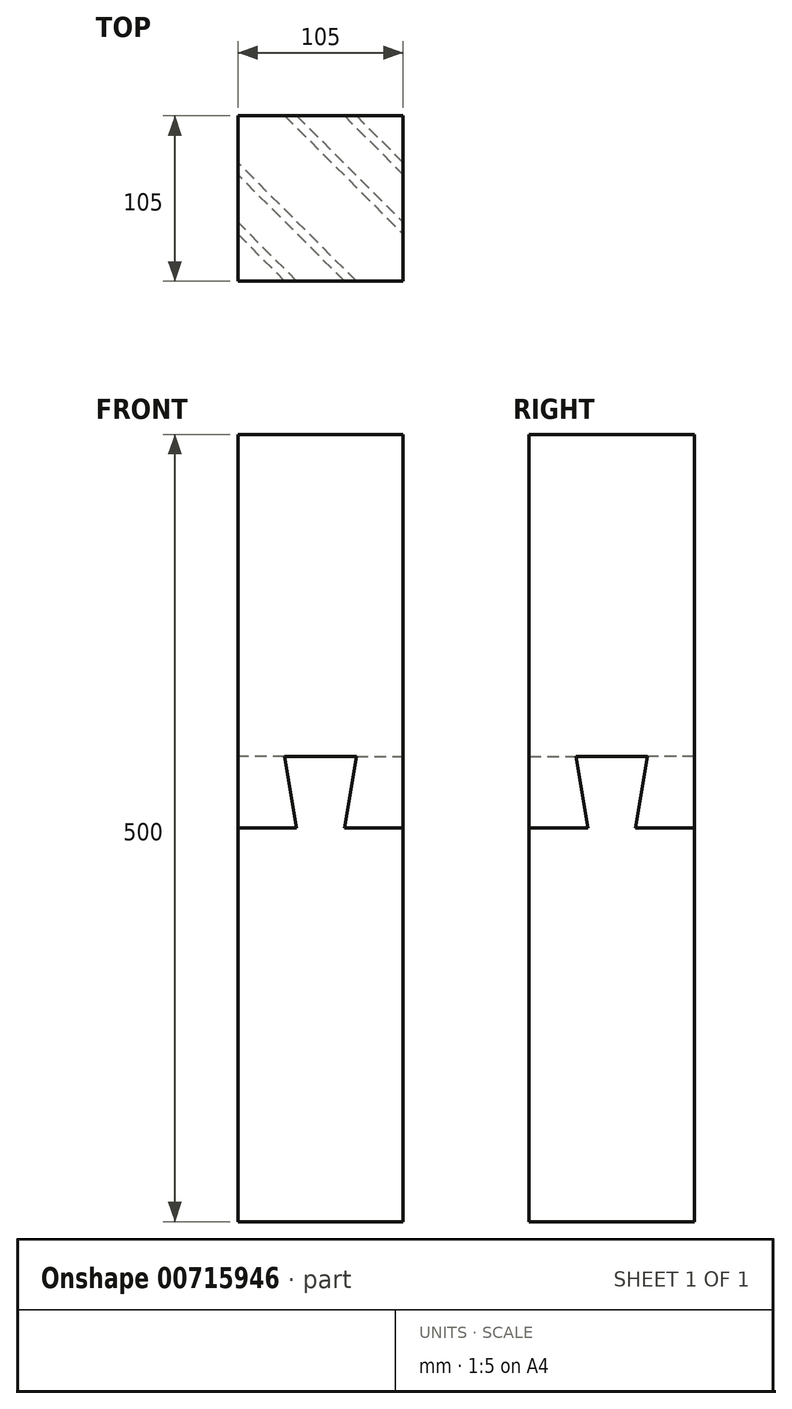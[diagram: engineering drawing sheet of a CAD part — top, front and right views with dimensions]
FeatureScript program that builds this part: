
annotation { "Feature Type Name" : "Feature", "Feature Type Description" : "" }
export const myFeature = defineFeature(function(context is Context, id is Id, definition is map)
    precondition{}
    {
        {
            var Q0;
            Q0=qCreatedBy(makeId("Top.planeOp"),FACE);
            var sketch = newSketch(context, id + "F0", { "sketchPlane" : qUnion([Q0])});
            skLineSegment(sketch, "E0.bottom", {"start": v(52.5, 52.5) * mm, "end": v(-52.5, 52.5) * mm});
            skLineSegment(sketch, "E0.top", {"start": v(52.5, -52.5) * mm, "end": v(-52.5, -52.5) * mm});
            skLineSegment(sketch, "E0.left", {"start": v(52.5, 52.5) * mm, "end": v(52.5, -52.5) * mm});
            skLineSegment(sketch, "E0.right", {"start": v(-52.5, 52.5) * mm, "end": v(-52.5, -52.5) * mm});
            skPoint(sketch, "E0.middle", {"position": v(0, 0) * mm});
            skSolve(sketch);
        }
        {
            var Q0;
            Q0=makeQuery(id+"F0.imprint","IMPRINT",FACE,{"disambiguationData":[TD([[makeQuery(id+"F0.imprint","IMPRINT",EDGE,{"derivedFrom":sQuery(id+"F0.wireOp",EDGE,"E0.bottom")}),1.0]])]});
            extrude(context, id + "F1", {"entities" : qUnion([Q0]), "oppositeDirection" : true, "depth" : 250 * mm, "offsetDistance" : 25 * mm});
        }
        {
            var Q0;
            Q0=makeQuery(id+"F1.opExtrude","SWEPT_FACE",FACE,{"disambiguationData":[OSD([sQuery(id+"F0.wireOp",EDGE,"E0.top")])]});
            var sketch = newSketch(context, id + "F2", { "sketchPlane" : qUnion([Q0])});
            skLineSegment(sketch, "E1", {"start": v(-22.73, 45.45) * mm, "end": v(22.73, 45.45) * mm});
            skLineSegment(sketch, "E2", {"start": v(22.73, 45.45) * mm, "end": v(15.15, 0) * mm});
            skLineSegment(sketch, "E3", {"start": v(15.15, 0) * mm, "end": v(-15.15, 0) * mm});
            skLineSegment(sketch, "E4", {"start": v(-15.15, 0) * mm, "end": v(-22.73, 45.45) * mm});
            skSolve(sketch);
        }
        {
            var Q0;
            Q0=makeQuery(id+"F1.opExtrude","SWEPT_FACE",FACE,{"disambiguationData":[OSD([sQuery(id+"F0.wireOp",EDGE,"E0.right")])]});
            var sketch = newSketch(context, id + "F3", { "sketchPlane" : qUnion([Q0])});
            skLineSegment(sketch, "E5", {"start": v(-22.72, 45.45) * mm, "end": v(22.73, 45.45) * mm});
            skLineSegment(sketch, "E6", {"start": v(22.73, 45.45) * mm, "end": v(15.15, 0) * mm});
            skLineSegment(sketch, "E7", {"start": v(15.15, 0) * mm, "end": v(-15.15, 0) * mm});
            skLineSegment(sketch, "E8", {"start": v(-15.15, 0) * mm, "end": v(-22.72, 45.45) * mm});
            skSolve(sketch);
        }
        {
            var Q1;
            Q1=makeQuery(id+"F2.imprint","IMPRINT",FACE,{"disambiguationData":[TD([[makeQuery(id+"F2.imprint","IMPRINT",EDGE,{"derivedFrom":sQuery(id+"F2.wireOp",EDGE,"E1")}),-1.0]])]});
            var Q2;
            Q2=makeQuery(id+"F3.imprint","IMPRINT",FACE,{"disambiguationData":[TD([[makeQuery(id+"F3.imprint","IMPRINT",EDGE,{"derivedFrom":sQuery(id+"F3.wireOp",EDGE,"E5")}),-1.0]])]});
            loft(context, id + "F4", {"operationType" : NewBodyOperationType.ADD, "sheetProfilesArray" : [{ "sheetProfileEntities" : qUnion([Q1]) }, { "sheetProfileEntities" : qUnion([Q2]) }]});
        }
        {
            var Q0;
            Q0=makeQuery(id+"F1.opExtrude","SWEPT_FACE",FACE,{"disambiguationData":[OSD([sQuery(id+"F0.wireOp",EDGE,"E0.bottom")])]});
            var sketch = newSketch(context, id + "F5", { "sketchPlane" : qUnion([Q0])});
            skLineSegment(sketch, "E9.0", {"start": v(15.15, 0) * mm, "end": v(22.73, 45.45) * mm});
            skLineSegment(sketch, "E10.0", {"start": v(22.73, 45.45) * mm, "end": v(-22.73, 45.45) * mm});
            skLineSegment(sketch, "E11.0", {"start": v(-22.73, 45.45) * mm, "end": v(-15.15, 0) * mm});
            skSolve(sketch);
        }
        {
            var Q0;
            Q0=makeQuery(id+"F1.opExtrude","SWEPT_FACE",FACE,{"disambiguationData":[OSD([sQuery(id+"F0.wireOp",EDGE,"E0.left")])]});
            var sketch = newSketch(context, id + "F6", { "sketchPlane" : qUnion([Q0])});
            skLineSegment(sketch, "E12.0", {"start": v(-15.15, 0) * mm, "end": v(-22.73, 45.45) * mm});
            skLineSegment(sketch, "E13.0", {"start": v(-22.73, 45.45) * mm, "end": v(22.72, 45.45) * mm});
            skLineSegment(sketch, "E14.0", {"start": v(22.73, 45.45) * mm, "end": v(15.15, 0) * mm});
            skSolve(sketch);
        }
        {
            var Q1;
            {var subQ0=sQuery(id+"F5.wireOp",EDGE,"E9.0");Q1=makeQuery(id+"F5.imprint","IMPRINT",FACE,{"disambiguationData":[TD([[makeQuery(id+"F5.imprint","IMPRINT",EDGE,{"derivedFrom":subQ0}),1.0]])]});}
            var Q2;
            {var subQ0=sQuery(id+"F6.wireOp",EDGE,"E12.0");Q2=makeQuery(id+"F6.imprint","IMPRINT",FACE,{"disambiguationData":[TD([[makeQuery(id+"F6.imprint","IMPRINT",EDGE,{"derivedFrom":subQ0}),-1.0]])]});}
            loft(context, id + "F7", {"operationType" : NewBodyOperationType.ADD, "sheetProfilesArray" : [{ "sheetProfileEntities" : qUnion([Q1]) }, { "sheetProfileEntities" : qUnion([Q2]) }]});
        }
        {
            var Q0;
            Q0=qCreatedBy(makeId("Top.planeOp"),FACE);
            var sketch = newSketch(context, id + "F8", { "sketchPlane" : qUnion([Q0])});
            skLineSegment(sketch, "E15.bottom", {"start": v(-52.5, -52.5) * mm, "end": v(52.5, -52.5) * mm});
            skLineSegment(sketch, "E15.top", {"start": v(-52.5, 52.5) * mm, "end": v(52.5, 52.5) * mm});
            skLineSegment(sketch, "E15.left", {"start": v(-52.5, -52.5) * mm, "end": v(-52.5, 52.5) * mm});
            skLineSegment(sketch, "E15.right", {"start": v(52.5, -52.5) * mm, "end": v(52.5, 52.5) * mm});
            skSolve(sketch);
        }
        {
            var Q0;
            Q0 = qSketchRegion(id + "F8", true);
            extrude(context, id + "F9", {"entities" : qUnion([Q0]), "depth" : 250 * mm, "offsetDistance" : 25 * mm});
        }
        {
            var Q0;
            Q0=makeQuery(id+"F1.opExtrude","SWEPT_BODY",BODY,{"disambiguationData":[OSD([sQuery(id+"F0.wireOp",EDGE,"E0.bottom"),sQuery(id+"F0.wireOp",EDGE,"E0.top"),sQuery(id+"F0.wireOp",EDGE,"E0.left"),sQuery(id+"F0.wireOp",EDGE,"E0.right")])]});
            var Q1;
            Q1=makeQuery(id+"F9.opExtrude","SWEPT_BODY",BODY,{"disambiguationData":[OSD([sQuery(id+"F8.wireOp",EDGE,"E15.bottom"),sQuery(id+"F8.wireOp",EDGE,"E15.top"),sQuery(id+"F8.wireOp",EDGE,"E15.left"),sQuery(id+"F8.wireOp",EDGE,"E15.right")])]});
            booleanBodies(context, id + "F10", {"operationType" : BooleanOperationType.SUBTRACTION, "tools" : qUnion([Q0]), "targets" : qUnion([Q1]), "keepTools" : true});
        }
    });
